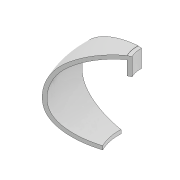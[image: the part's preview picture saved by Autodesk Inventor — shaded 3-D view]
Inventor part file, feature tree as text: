
AUTODESK INVENTOR PART (.ipt)
format: ipt  version: 2022 (Build 260153000, 153)  size: 333,312 bytes
history: native  units: mm
features: sketch x7, extrude x6, thicken_offset x2, plane x2, revolve x1, projected_geometry x1
ambient origin geometry x8: Origin, YZ Plane, XZ Plane, XY Plane, X Axis, Y Axis, Z Axis, Center Point
bodies: Solid1 (feature_tree)
feature tree (19):
  revolve  "Revolution1"  [1 undecoded]
  thicken_offset  "Thicken1"
  thicken_offset  "Thicken2"
  extrude  "Extrusion9"  Depth=27.925268mm
  extrude  "Extrusion2"  Depth=2.1mm
  extrude  "Extrusion3"  Depth=4.5mm
  plane  "Work Plane2"
  extrude  "Extrusion7"  Depth=18.0mm
  plane  "Work Plane3"
  extrude  "Extrusion10"  Depth=6.981317mm
  extrude  "Extrusion11"  Depth=30.0mm
  sketch  "Sketch1"  dims[d2=45.0mm d3=40.0mm]
  sketch  "Sketch3"  dims[d4=2.0mm d5=27.925268mm]
  sketch  "Sketch4"  dims[d9=2.1mm d10=2.1mm]
  projected_geometry  "Projected Loop1"
  sketch  "Sketch8"  dims[d11=23.6mm d12=4.5mm]
  sketch  "Sketch10"  dims[d13=23.6mm d14=18.0mm]
  sketch  "Sketch11"  dims[d15=100.0mm d16=0.0mm d17=6.981317mm]
  sketch  "Sketch12"  dims[d18=100.0mm d19=0.0mm d38=30.0mm d39=30.0mm d40=20.0mm d41=0.0mm d42=33.9mm d50=4.5mm d51=4.5mm d52=4.5mm d53=2.5mm d54=50.0mm d55=10.0mm d56=0.0mm d57=2.0mm d58=30.0deg d59=9.6mm d60=0.0mm d61=1000.0mm d62=0.0mm]
note: 1 required parameter value undecoded (feature->parameter linkage not recoverable at this tier; creation-order binding heuristic only, values carry confidence <= 0.55)
